# Revit family: Gira_222000
name_source: partatom
category: Elektroinstallationen
revit_build: Autodesk Revit 2017 (Build: 20160225_1515(x64)
units: mm (PartAtom-declared; Revit-internal decimal feet)

## family parameters
Basisbauteil = Fläche
Beim Laden mit Abzugskörper schneiden = Nein
Bemaßung runder Anschluss = Durchmesser verwenden
Beschriftungsausrichtung beibehalten = Nein
Gemeinsam genutzt = Nein
Raumberechnungspunkt = Nein
Teiletyp = Normal

## types (1)
- Gira_222000
    BIM = https://media.stage.bim.site
    Beschreibung = Pres.det.Mini Std KNX,KNX presence detector Mini Standard,,,Presence detector for presence monitoring (operating mode: presence detector), for motion detection (operating mode: ceiling sentinel) or for monitoring with alarm telegrams (operating mode: alarm device) indoors or outdoors. With their subtle and flat design and flexible installation concept, presence detectors Mini are particularly suitable for properties with high architectural demands.,,Features:,- Extreme flat installation.,- Terminal mounting on suspended ceilings.,- Ceiling mounting on stable ceilings in device box in accordance with DIN 49073 using optional accessories.,- Surface mounted installation in surface-mounted box (optional accessories).,- Protection type IP44 allows installation outdoors and in humid rooms.,- The colour emphasis of the design rings enables their colours to be adapted to the wall or ceiling.,- When the design ring has been removed, all the operating elements (e.g. the programming button) of the device can be conveniently accessed from the front. Thus, removal is not necessary for subsequent adjustment or programming via the ETS.,- Ceiling-mounted device with integrated KNX bus coupler.,- PIR sensors: three sensors, integrated brightness sensor.,- Sensitivity of the motion detection can be set manually using an adjuster.,- Sensitivity can be configured by ETS.,- Sensitivity adjuster on the device can be deactivated using the software.,- Indication of motion detection (permanent or only during walking test).,- One function block configurable.,- Adjustable operating mode: ceiling sentinel, presence detector, alarm device.,- Individual device, main unit, auxiliary unit can be set.,- Operating mode for individual device or main unit: automatic, semi-automatic (manual ON   automatic OFF, or automatic ON   manual OFF).,- Two outputs (for function: ceiling sentinel, presence detector).,- Output (for function: ceiling sentinel, presence detector): switching, staircase function, switching with forced setting, dimming value transmitter, light scene auxiliary unit, temperature value transmitter, brightness value transmitter, temperature operating mode.,- Twilight stage can be set using external communication object or teach-in.,- Additional transmission delay via external communication object.,- Adaptive delay time (self-teaching additional transmission delay),- Short-term presence function.,- Feedback of twilight stage.,- Block function.,- Manual actuation using pushbutton sensor (separate communication object).,- Switch-off brightness (for presence detectors) via teach-in.,- Measurement of time period after last motion.,,Notes :,- The presence detector Mini is not suitable for alarm messages in VdS-compliant alarm systems.
    Bus system KNX = Ja
    Bus system KNX radio = Nein
    Bus system LON = Nein
    Bus system Powernet = Nein
    Bus system radio frequent = Nein
    Colour = White
    Data sheet = https://katalog.gira.de
    GTIN = 4010337014683
    HAN = 222000
    Hersteller = Gira
    Material = Other
    Material quality = Other
    Model = Presence detector
    Mounting method = Surface mounted (plaster)
    Other bus systems = None
    Productwebsite = http://katalog.gira.de
    Surface finishing = Not applicable
    Surface protection = Other
    Transparent = Nein
    Typname = Pres.detec.Mini Standard KNX
    URL = https://www.gira.de
    Vorgabe-Ansicht = 1219 mm

## geometry (parser evidence)
native form markers: Sweep x1
no freeform markers — native parametric forms only
